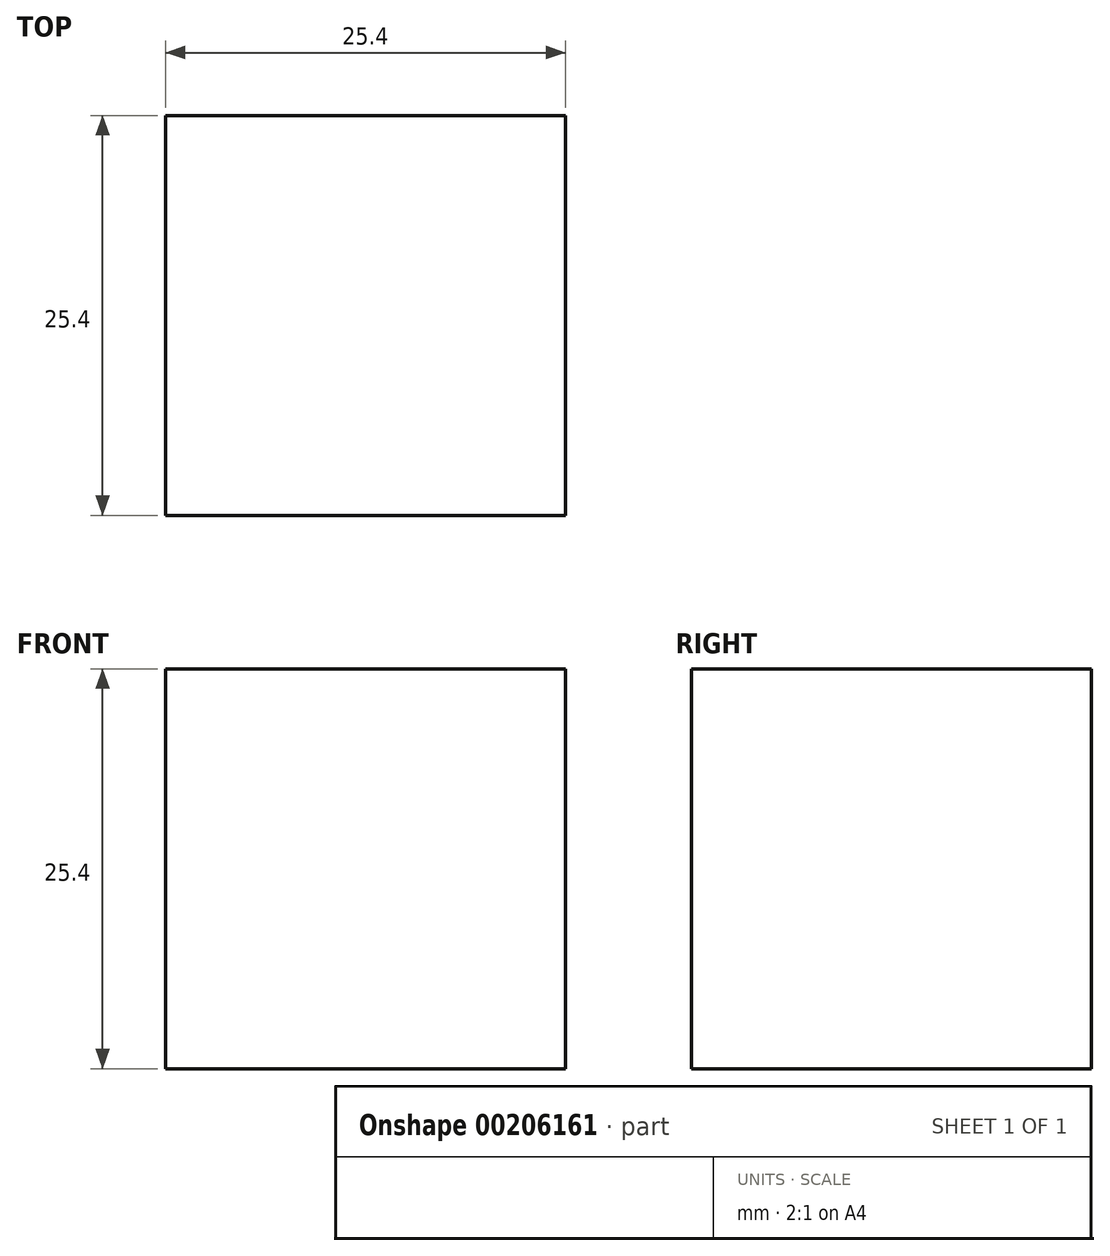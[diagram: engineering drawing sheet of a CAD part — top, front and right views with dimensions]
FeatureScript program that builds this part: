
annotation { "Feature Type Name" : "Feature", "Feature Type Description" : "" }
export const myFeature = defineFeature(function(context is Context, id is Id, definition is map)
    precondition{}
    {
        {
            var Q0;
            Q0=qCreatedBy(makeId("Top.planeOp"),FACE);
            var sketch = newSketch(context, id + "F0", { "sketchPlane" : qUnion([Q0])});
            skLineSegment(sketch, "E0.bottom", {"start": v(12.7, 12.7) * mm, "end": v(-12.7, 12.7) * mm});
            skLineSegment(sketch, "E0.top", {"start": v(12.7, -12.7) * mm, "end": v(-12.7, -12.7) * mm});
            skLineSegment(sketch, "E0.left", {"start": v(12.7, 12.7) * mm, "end": v(12.7, -12.7) * mm});
            skLineSegment(sketch, "E0.right", {"start": v(-12.7, 12.7) * mm, "end": v(-12.7, -12.7) * mm});
            skPoint(sketch, "E0.middle", {"position": v(0, 0) * mm});
            skSolve(sketch);
        }
        {
            var Q0;
            Q0 = qSketchRegion(id + "F0", true);
            extrude(context, id + "F1", {"entities" : qUnion([Q0]), "depth" : 25.4 * mm});
        }
    });
